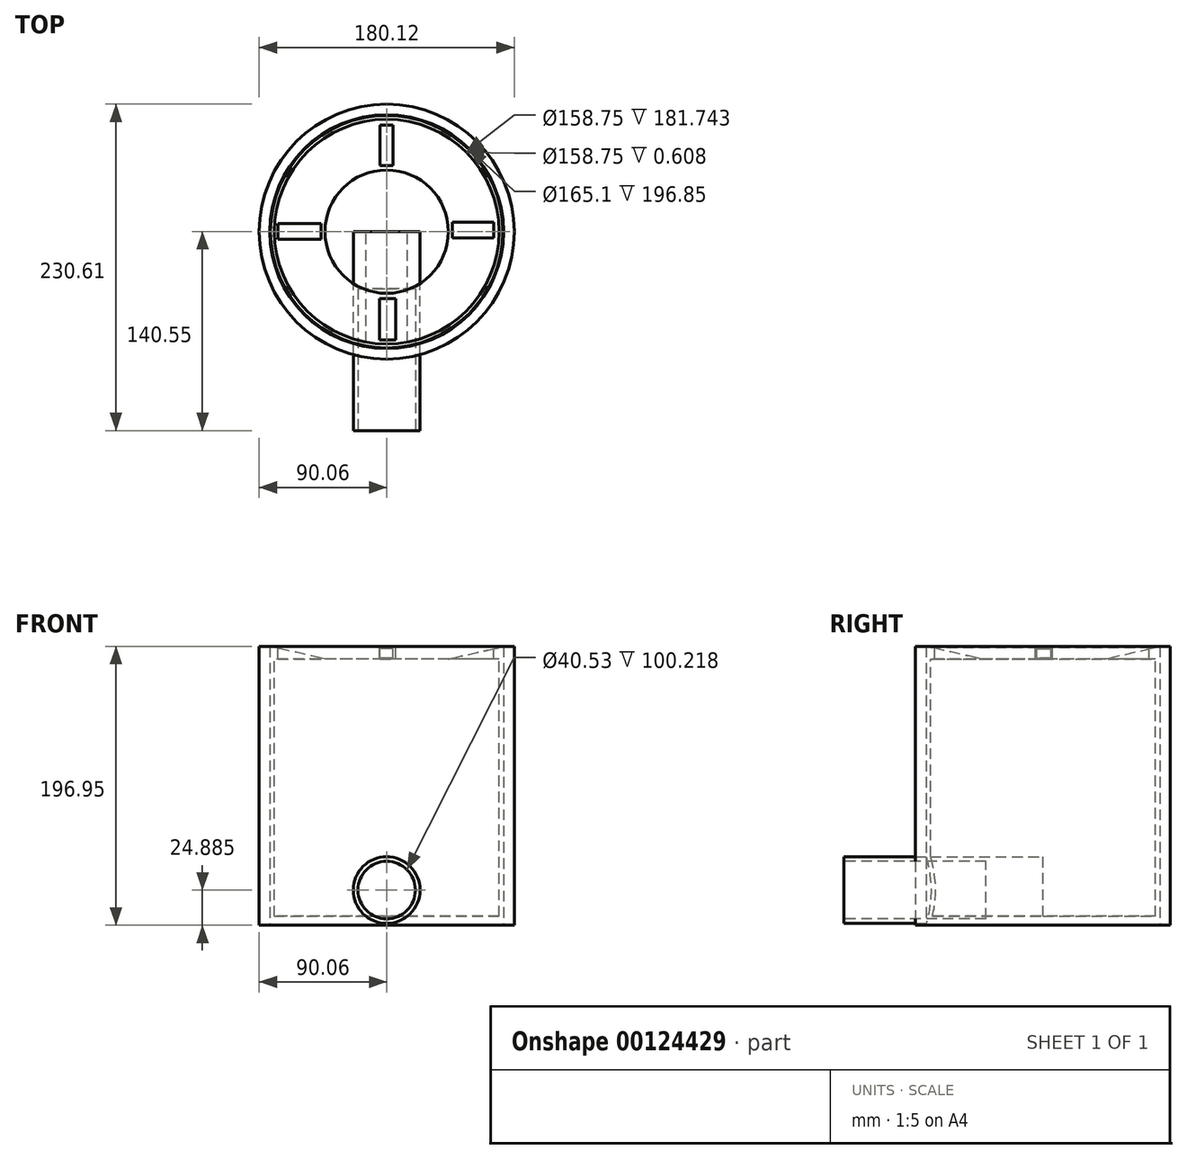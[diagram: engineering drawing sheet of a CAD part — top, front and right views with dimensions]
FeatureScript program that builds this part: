
annotation { "Feature Type Name" : "Feature", "Feature Type Description" : "" }
export const myFeature = defineFeature(function(context is Context, id is Id, definition is map)
    precondition{}
    {
        {
            var Q0;
            Q0=qCreatedBy(makeId("Top.planeOp"),FACE);
            var sketch = newSketch(context, id + "F0", { "sketchPlane" : qUnion([Q0])});
            skCircle(sketch, "E0", {"center": v(0, 0) * mm, "radius": 82.55 * mm});
            skSolve(sketch);
        }
        {
            var Q0;
            Q0=makeQuery(id+"F0.imprint","IMPRINT",FACE,{"disambiguationData":[TD([[makeQuery(id+"F0.imprint","IMPRINT",EDGE,{"derivedFrom":sQuery(id+"F0.wireOp",EDGE,"E0")}),1.0]])]});
            extrude(context, id + "F1", {"entities" : qUnion([Q0]), "depth" : 196.85 * mm});
        }
        {
            var Q0;
            Q0=makeQuery(id+"F1.opExtrude","CAP_FACE",FACE,{"disambiguationData":[OSD([sQuery(id+"F0.wireOp",EDGE,"E0")])],"isStart":false});
            var sketch = newSketch(context, id + "F2", { "sketchPlane" : qUnion([Q0])});
            skCircle(sketch, "E1", {"center": v(0, 0) * mm, "radius": 79.37 * mm});
            skSolve(sketch);
        }
        {
            var Q0;
            Q0=makeQuery(id+"F2.imprint","IMPRINT",FACE,{"disambiguationData":[TD([[makeQuery(id+"F2.imprint","IMPRINT",EDGE,{"derivedFrom":sQuery(id+"F2.wireOp",EDGE,"E1")}),1.0]])]});
            extrude(context, id + "F3", {"entities" : qUnion([Q0]), "operationType" : NewBodyOperationType.REMOVE, "oppositeDirection" : true, "depth" : 190.5 * mm});
        }
        {
            var Q0;
            Q0=qCreatedBy(makeId("Top.planeOp"),FACE);
            cPlane(context, id + "F4", {"entities" : qUnion([Q0]), "cplaneType" : CPlaneType.OFFSET, "offset" : 196.85 * mm, "width" : 152.4 * mm, "height" : 152.4 * mm});
        }
        {
            var Q0;
            Q0=qCreatedBy(id+"F4.planeOp",FACE);
            var sketch = newSketch(context, id + "F5", { "sketchPlane" : qUnion([Q0])});
            skArc(sketch, "E2", {"start": v(-6.1, 80.91) * mm, "mid": v(-57.77, 56.98) * mm, "end": v(-80.99, 5) * mm});
            skArc(sketch, "E3", {"start": v(4.7, 80.91) * mm, "mid": v(56.75, 57.87) * mm, "end": v(80.8, 6.28) * mm});
            skArc(sketch, "E4", {"start": v(-3.56, -80.55) * mm, "mid": v(-56.58, -57.44) * mm, "end": v(-80.5, -4.77) * mm});
            skArc(sketch, "E5", {"start": v(4.16, -80.96) * mm, "mid": v(57.39, -57.26) * mm, "end": v(80.97, -3.98) * mm});
            skSolve(sketch);
        }
        {
            var Q0;
            Q0=sQuery(id+"F5.wireOp",EDGE,"E5");
            var Q1;
            Q1=sQuery(id+"F5.wireOp",EDGE,"E3");
            var Q2;
            Q2=sQuery(id+"F5.wireOp",EDGE,"E2");
            var Q3;
            Q3=sQuery(id+"F5.wireOp",EDGE,"E4");
            extrude(context, id + "F6", {"bodyType" : ToolBodyType.SURFACE, "surfaceEntities" : qUnion([Q0, Q1, Q2, Q3]), "depth" : 19.05 * mm});
        }
        {
            var Q0;
            Q0=qCreatedBy(makeId("Front.planeOp"),FACE);
            var sketch = newSketch(context, id + "F7", { "sketchPlane" : qUnion([Q0])});
            skLineSegment(sketch, "E6", {"start": v(82.5, 196.95) * mm, "end": v(43.56, 188.1) * mm});
            skLineSegment(sketch, "E7", {"start": v(43.56, 188.1) * mm, "end": v(82.54, 188.1) * mm});
            skLineSegment(sketch, "E8", {"start": v(82.54, 188.1) * mm, "end": v(82.5, 196.95) * mm});
            skSolve(sketch);
        }
        {
            var Q0;
            Q0 = qSketchRegion(id + "F7", true);
            var Q1;
            Q1=makeQuery(id+"F3.boolean.opBoolean","COPY",FACE,{"derivedFrom":makeQuery(id+"F3.opExtrude","SWEPT_FACE",FACE,{"disambiguationData":[OSD([sQuery(id+"F2.wireOp",EDGE,"E1")])]})});
            revolve(context, id + "F8", {"operationType" : NewBodyOperationType.ADD, "entities" : qUnion([Q0]), "axis" : qUnion([Q1]), "revolveType" : RevolveType.FULL});
        }
        {
            var Q0;
            Q0=qCreatedBy(id+"F4.planeOp",FACE);
            var sketch = newSketch(context, id + "F9", { "sketchPlane" : qUnion([Q0])});
            skLineSegment(sketch, "E9.bottom", {"start": v(-4.75, 75.14) * mm, "end": v(4.41, 75.14) * mm});
            skLineSegment(sketch, "E9.top", {"start": v(-4.75, 46.65) * mm, "end": v(4.41, 46.65) * mm});
            skLineSegment(sketch, "E9.left", {"start": v(-4.75, 75.14) * mm, "end": v(-4.75, 46.65) * mm});
            skLineSegment(sketch, "E9.right", {"start": v(4.41, 75.14) * mm, "end": v(4.41, 46.65) * mm});
            skLineSegment(sketch, "E10.bottom", {"start": v(75.48, 6.78) * mm, "end": v(46.3, 6.78) * mm});
            skLineSegment(sketch, "E10.top", {"start": v(75.48, -4.41) * mm, "end": v(46.3, -4.41) * mm});
            skLineSegment(sketch, "E10.left", {"start": v(75.48, 6.78) * mm, "end": v(75.48, -4.41) * mm});
            skLineSegment(sketch, "E10.right", {"start": v(46.3, 6.78) * mm, "end": v(46.3, -4.41) * mm});
            skLineSegment(sketch, "E11.bottom", {"start": v(-76.84, -5.43) * mm, "end": v(-46.3, -5.43) * mm});
            skLineSegment(sketch, "E11.top", {"start": v(-76.84, 5.77) * mm, "end": v(-46.3, 5.77) * mm});
            skLineSegment(sketch, "E11.left", {"start": v(-76.84, -5.43) * mm, "end": v(-76.84, 5.77) * mm});
            skLineSegment(sketch, "E11.right", {"start": v(-46.3, -5.43) * mm, "end": v(-46.3, 5.77) * mm});
            skLineSegment(sketch, "E12.bottom", {"start": v(6.45, -76.5) * mm, "end": v(-5.09, -76.5) * mm});
            skLineSegment(sketch, "E12.top", {"start": v(6.45, -47.32) * mm, "end": v(-5.09, -47.32) * mm});
            skLineSegment(sketch, "E12.left", {"start": v(6.45, -76.5) * mm, "end": v(6.45, -47.32) * mm});
            skLineSegment(sketch, "E12.right", {"start": v(-5.09, -76.5) * mm, "end": v(-5.09, -47.32) * mm});
            skSolve(sketch);
        }
        {
            var Q0;
            Q0 = qSketchRegion(id + "F9", true);
            extrude(context, id + "F10", {"entities" : qUnion([Q0]), "operationType" : NewBodyOperationType.REMOVE, "oppositeDirection" : true, "depth" : 50.8 * mm});
        }
        {
            var Q0;
            Q0=qCreatedBy(makeId("Front.planeOp"),FACE);
            var sketch = newSketch(context, id + "F11", { "sketchPlane" : qUnion([Q0])});
            skCircle(sketch, "E13", {"center": v(0, 24.89) * mm, "radius": 23.59 * mm});
            skSolve(sketch);
        }
        {
            var Q0;
            Q0 = qSketchRegion(id + "F11", true);
            extrude(context, id + "F12", {"entities" : qUnion([Q0]), "operationType" : NewBodyOperationType.ADD, "depth" : 140.55 * mm});
        }
        {
            var Q0;
            Q0=makeQuery(id+"F12.opExtrude","CAP_FACE",FACE,{"disambiguationData":[OSD([sQuery(id+"F11.wireOp",EDGE,"E13")])],"isStart":false});
            var sketch = newSketch(context, id + "F13", { "sketchPlane" : qUnion([Q0])});
            skCircle(sketch, "E14", {"center": v(0, 24.89) * mm, "radius": 20.27 * mm});
            skSolve(sketch);
        }
        {
            var Q0;
            Q0=makeQuery(id+"F13.imprint","IMPRINT",FACE,{"disambiguationData":[TD([[makeQuery(id+"F13.imprint","IMPRINT",EDGE,{"derivedFrom":sQuery(id+"F13.wireOp",EDGE,"E14")}),1.0]])]});
            extrude(context, id + "F14", {"entities" : qUnion([Q0]), "operationType" : NewBodyOperationType.REMOVE, "oppositeDirection" : true, "depth" : 100.22 * mm});
        }
        {
            var Q0;
            Q0=qCreatedBy(makeId("Top.planeOp"),FACE);
            var sketch = newSketch(context, id + "F15", { "sketchPlane" : qUnion([Q0])});
            skCircle(sketch, "E15", {"center": v(0, 0) * mm, "radius": 90.06 * mm});
            skCircle(sketch, "E16", {"center": v(0, 0) * mm, "radius": 82.55 * mm});
            skSolve(sketch);
        }
        {
            var Q0;
            Q0=makeQuery(id+"F15.imprint","IMPRINT",FACE,{"disambiguationData":[TD([[makeQuery(id+"F15.imprint","IMPRINT",EDGE,{"derivedFrom":sQuery(id+"F15.wireOp",EDGE,"E15")}),1.0]])]});
            extrude(context, id + "F16", {"entities" : qUnion([Q0]), "depth" : 196.85 * mm});
        }
    });
